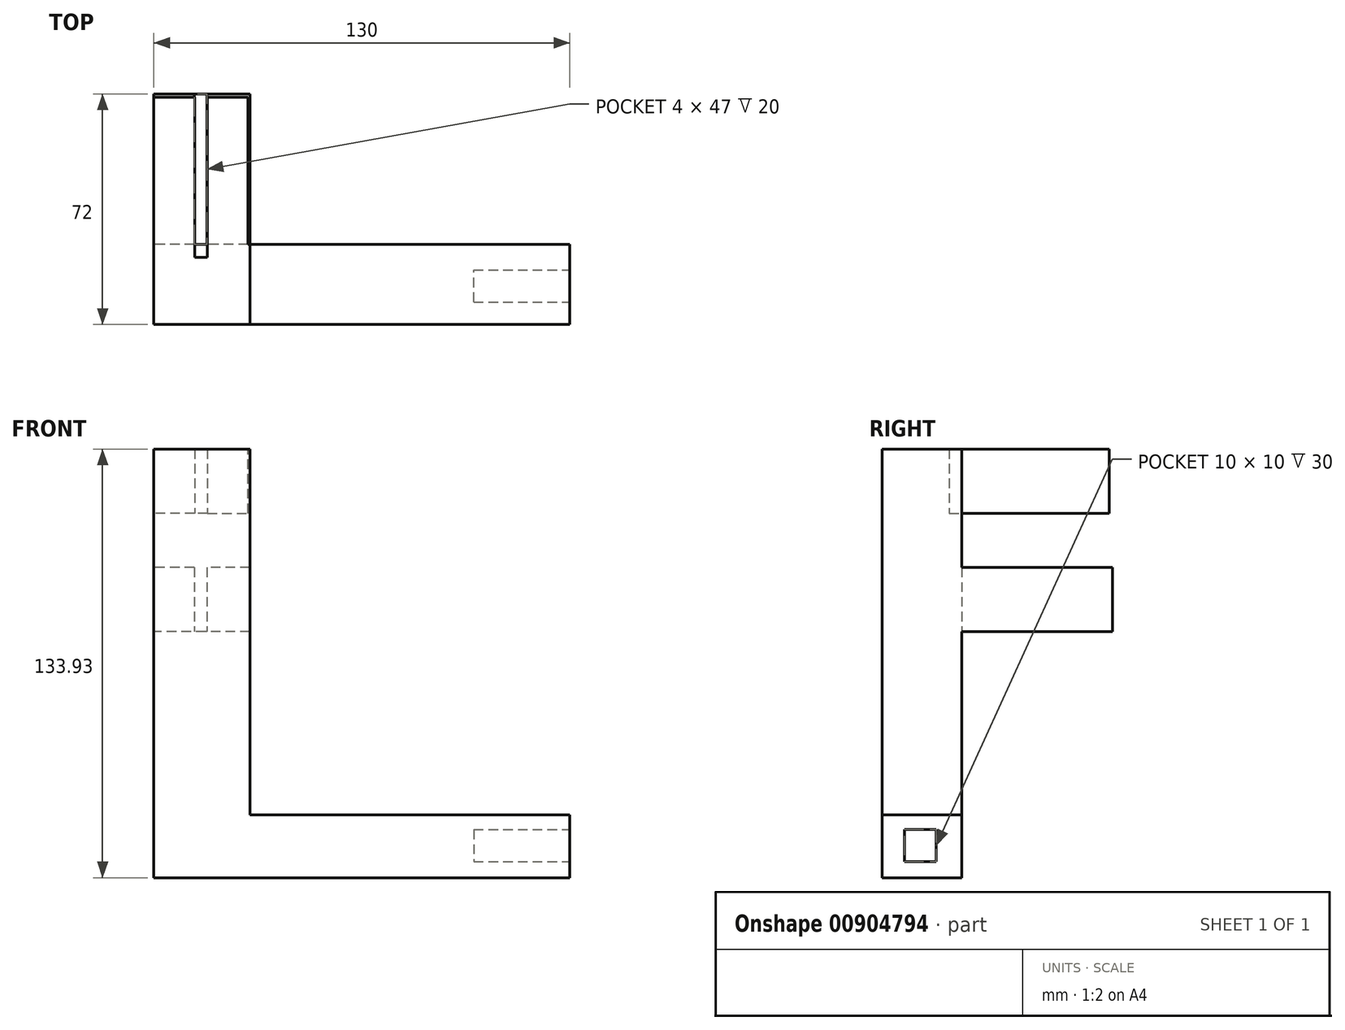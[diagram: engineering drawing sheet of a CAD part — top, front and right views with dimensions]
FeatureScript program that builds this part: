
annotation { "Feature Type Name" : "Feature", "Feature Type Description" : "" }
export const myFeature = defineFeature(function(context is Context, id is Id, definition is map)
    precondition{}
    {
        {
            var Q0;
            Q0=qCreatedBy(makeId("Front.planeOp"),FACE);
            var sketch = newSketch(context, id + "F0", { "sketchPlane" : qUnion([Q0])});
            skLineSegment(sketch, "E0", {"start": v(40.24, -76.64) * mm, "end": v(40.24, -76.5) * mm});
            skLineSegment(sketch, "E1", {"start": v(40.24, -76.64) * mm, "end": v(-89.76, -76.64) * mm});
            skLineSegment(sketch, "E2", {"start": v(-89.76, -76.64) * mm, "end": v(-89.76, 57.3) * mm});
            skLineSegment(sketch, "E3", {"start": v(-89.76, 57.3) * mm, "end": v(-59.76, 57.3) * mm});
            skLineSegment(sketch, "E4", {"start": v(-59.76, -57) * mm, "end": v(-59.76, 57.3) * mm});
            skLineSegment(sketch, "E5", {"start": v(-59.76, -57) * mm, "end": v(40.24, -57) * mm});
            skLineSegment(sketch, "E6", {"start": v(40.24, -57) * mm, "end": v(40.24, -76.5) * mm});
            skSolve(sketch);
        }
        {
            var Q0;
            Q0=makeQuery(id+"F0.imprint","IMPRINT",FACE,{"disambiguationData":[TD([[makeQuery(id+"F0.imprint","IMPRINT",EDGE,{"derivedFrom":sQuery(id+"F0.wireOp",EDGE,"E0")}),1.0]])]});
            extrude(context, id + "F1", {"entities" : qUnion([Q0]), "depth" : 25 * mm, "offsetDistance" : 25 * mm});
        }
        {
            var Q0;
            Q0=makeQuery(id+"F1.opExtrude","SWEPT_FACE",FACE,{"disambiguationData":[OSD([sQuery(id+"F0.wireOp",EDGE,"E3")])]});
            var sketch = newSketch(context, id + "F2", { "sketchPlane" : qUnion([Q0])});
            skLineSegment(sketch, "E7.bottom", {"start": v(-89.76, 46) * mm, "end": v(-60.31, 46) * mm});
            skLineSegment(sketch, "E7.top", {"start": v(-89.76, -9) * mm, "end": v(-60.31, -9) * mm});
            skLineSegment(sketch, "E7.left", {"start": v(-89.76, 46) * mm, "end": v(-89.76, -9) * mm});
            skLineSegment(sketch, "E7.right", {"start": v(-60.31, 46) * mm, "end": v(-60.31, -9) * mm});
            skSolve(sketch);
        }
        {
            var Q0;
            {var subQ0=sQuery(id+"F2.wireOp",EDGE,"E7.top");Q0=makeQuery(id+"F2.imprint","IMPRINT",FACE,{"disambiguationData":[TD([[makeQuery(id+"F2.imprint","IMPRINT",EDGE,{"derivedFrom":subQ0}),1.0]])]});}
            var Q1;
            {var subQ0=sQuery(id+"F2.wireOp",EDGE,"E7.bottom");Q1=makeQuery(id+"F2.imprint","IMPRINT",FACE,{"disambiguationData":[TD([[makeQuery(id+"F2.imprint","IMPRINT",EDGE,{"derivedFrom":subQ0}),-1.0]])]});}
            extrude(context, id + "F3", {"entities" : qUnion([Q0, Q1]), "operationType" : NewBodyOperationType.ADD, "oppositeDirection" : true, "depth" : 20 * mm, "offsetDistance" : 25 * mm});
        }
        {
            var Q0;
            Q0=makeQuery(id+"F3.opExtrude","SWEPT_FACE",FACE,{"disambiguationData":[OSD([sQuery(id+"F2.wireOp",EDGE,"E7.bottom")])]});
            var sketch = newSketch(context, id + "F4", { "sketchPlane" : qUnion([Q0])});
            skLineSegment(sketch, "E8.bottom", {"start": v(73.04, 57.3) * mm, "end": v(77.04, 57.3) * mm});
            skLineSegment(sketch, "E8.top", {"start": v(73.04, 37.3) * mm, "end": v(77.04, 37.3) * mm});
            skLineSegment(sketch, "E9", {"start": v(77.04, 57.3) * mm, "end": v(77.04, 37.3) * mm});
            skLineSegment(sketch, "E10", {"start": v(73.04, 57.3) * mm, "end": v(73.04, 37.3) * mm});
            skSolve(sketch);
        }
        {
            var Q0;
            Q0=makeQuery(id+"F4.imprint","IMPRINT",FACE,{"disambiguationData":[TD([[makeQuery(id+"F4.imprint","IMPRINT",EDGE,{"derivedFrom":sQuery(id+"F4.wireOp",EDGE,"E8.top")}),-1.0]])]});
            extrude(context, id + "F5", {"entities" : qUnion([Q0]), "operationType" : NewBodyOperationType.REMOVE, "oppositeDirection" : true, "depth" : 50 * mm, "offsetDistance" : 25 * mm});
        }
        {
            var Q0;
            Q0=makeQuery(id+"F1.opExtrude","CAP_FACE",FACE,{"disambiguationData":[OSD([sQuery(id+"F0.wireOp",EDGE,"E0"),sQuery(id+"F0.wireOp",EDGE,"E1"),sQuery(id+"F0.wireOp",EDGE,"E2"),sQuery(id+"F0.wireOp",EDGE,"E3"),sQuery(id+"F0.wireOp",EDGE,"E4"),sQuery(id+"F0.wireOp",EDGE,"E5"),sQuery(id+"F0.wireOp",EDGE,"E6")])],"isStart":true});
            var sketch = newSketch(context, id + "F6", { "sketchPlane" : qUnion([Q0])});
            skLineSegment(sketch, "E11", {"start": v(59.76, 20.3) * mm, "end": v(89.9, 20.3) * mm});
            skLineSegment(sketch, "E12", {"start": v(59.76, 20.3) * mm, "end": v(59.76, 0.3) * mm});
            skLineSegment(sketch, "E13", {"start": v(89.9, 20.3) * mm, "end": v(89.9, 0.3) * mm});
            skLineSegment(sketch, "E14", {"start": v(59.76, 0.3) * mm, "end": v(89.9, 0.3) * mm});
            skLineSegment(sketch, "E15.bottom", {"start": v(73.13, 20.3) * mm, "end": v(77.13, 20.3) * mm});
            skLineSegment(sketch, "E16", {"start": v(77.13, 20.3) * mm, "end": v(77.13, 0.3) * mm});
            skLineSegment(sketch, "E17", {"start": v(73.13, 20.3) * mm, "end": v(73.13, 0.3) * mm});
            skLineSegment(sketch, "E18", {"start": v(73.13, 0.3) * mm, "end": v(77.13, 0.3) * mm});
            skSolve(sketch);
        }
        {
            var Q0;
            {var subQ0=sQuery(id+"F6.wireOp",EDGE,"E12");Q0=makeQuery(id+"F6.imprint","IMPRINT",FACE,{"disambiguationData":[TD([[makeQuery(id+"F6.imprint","IMPRINT",EDGE,{"derivedFrom":subQ0}),-1.0]])]});}
            var Q1;
            {var subQ0=sQuery(id+"F6.wireOp",EDGE,"E16");Q1=makeQuery(id+"F6.imprint","IMPRINT",FACE,{"disambiguationData":[TD([[makeQuery(id+"F6.imprint","IMPRINT",EDGE,{"derivedFrom":subQ0}),1.0]])]});}
            extrude(context, id + "F7", {"entities" : qUnion([Q0, Q1]), "operationType" : NewBodyOperationType.ADD, "depth" : 47 * mm, "offsetDistance" : 25 * mm});
        }
        {
            var Q0;
            Q0=makeQuery(id+"F1.opExtrude","SWEPT_FACE",FACE,{"disambiguationData":[OSD([sQuery(id+"F0.wireOp",EDGE,"E0"),sQuery(id+"F0.wireOp",EDGE,"E6")])]});
            var sketch = newSketch(context, id + "F8", { "sketchPlane" : qUnion([Q0])});
            skLineSegment(sketch, "E19.bottom", {"start": v(-18, -61.64) * mm, "end": v(-8, -61.64) * mm});
            skLineSegment(sketch, "E19.top", {"start": v(-18, -71.64) * mm, "end": v(-8, -71.64) * mm});
            skLineSegment(sketch, "E19.left", {"start": v(-18, -61.64) * mm, "end": v(-18, -71.64) * mm});
            skLineSegment(sketch, "E19.right", {"start": v(-8, -61.64) * mm, "end": v(-8, -71.64) * mm});
            skSolve(sketch);
        }
        {
            var Q0;
            Q0=makeQuery(id+"F8.imprint","IMPRINT",FACE,{"disambiguationData":[TD([[makeQuery(id+"F8.imprint","IMPRINT",EDGE,{"derivedFrom":sQuery(id+"F8.wireOp",EDGE,"E19.bottom")}),-1.0]])]});
            extrude(context, id + "F9", {"entities" : qUnion([Q0]), "operationType" : NewBodyOperationType.REMOVE, "oppositeDirection" : true, "depth" : 30 * mm, "offsetDistance" : 25 * mm});
        }
    });
